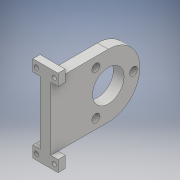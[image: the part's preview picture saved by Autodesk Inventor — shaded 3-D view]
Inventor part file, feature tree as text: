
AUTODESK INVENTOR PART (.ipt)
format: ipt  version: 2017 (Build 210142000, 142)  size: 191,488 bytes
history: native  units: mm
features: extrude x5, sketch x5
ambient origin geometry x8: Origin, YZ Plane, XZ Plane, XY Plane, X Axis, Y Axis, Z Axis, Center Point
bodies: Solid1 (feature_tree)
feature tree (10):
  extrude  "Extrusion1"  Depth=44.0mm
  extrude  "Extrusion2"  Depth=5.5mm
  extrude  "Extrusion3"  Depth=7.5mm TaperAngle=0.0deg
  extrude  "Extrusion5"  Depth=5.5mm
  extrude  "Extrusion6"  Depth=10.0mm TaperAngle=0.0deg
  sketch  "Sketch1"  dims[d0=22.0mm d1=44.0mm]
  sketch  "Sketch2"  dims[d2=35.0mm d3=5.5mm]
  sketch  "Sketch3"  dims[d4=30.0mm d6=360.0deg d8=7.5mm d9=0.0mm]
  sketch  "Sketch5"  dims[d10=35.0mm d11=5.5mm]
  sketch  "Sketch6"  dims[d12=30.0mm d14=360.0deg d16=10.0mm d17=0.0mm d18=40.0mm d19=90.0deg d20=50.0mm d21=25.0mm d22=5.0mm d23=30.0mm d24=5.0mm d25=60.0mm d26=5.0mm d27=7.5mm d28=0.0mm d41=5.0mm d42=12.5mm d43=0.0mm d44=0.0mm d45=3.0mm d46=3.0mm d47=3.0mm d48=3.0mm d49=5.0mm d50=0.0mm]
